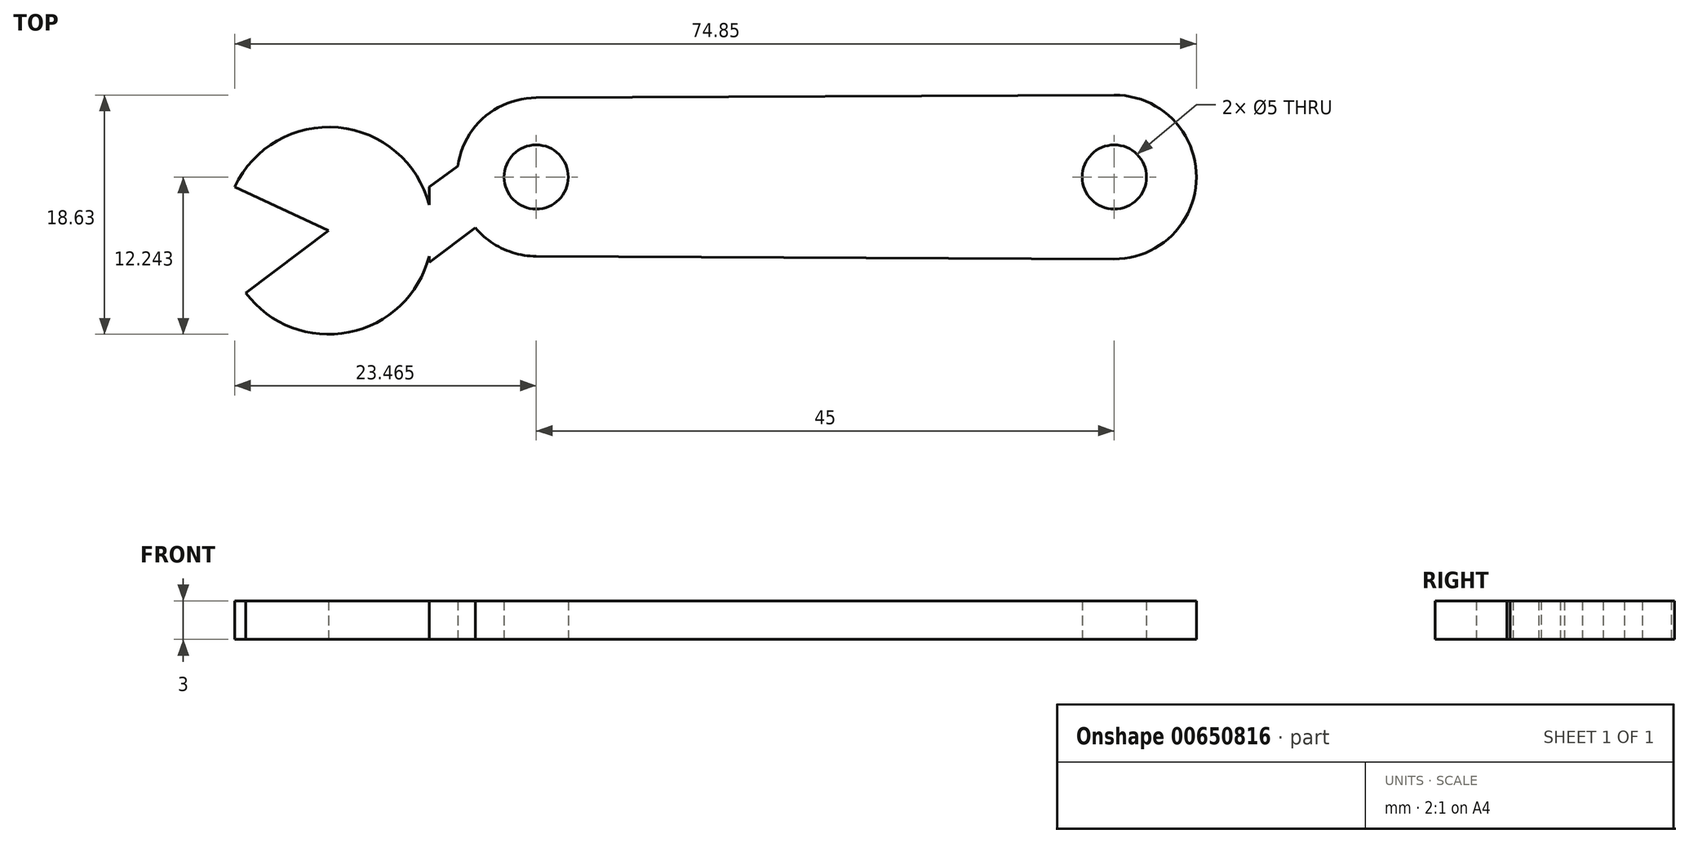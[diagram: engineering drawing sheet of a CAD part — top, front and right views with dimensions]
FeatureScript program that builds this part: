
annotation { "Feature Type Name" : "Feature", "Feature Type Description" : "" }
export const myFeature = defineFeature(function(context is Context, id is Id, definition is map)
    precondition{}
    {
        {
            var Q0;
            Q0=qCreatedBy(makeId("Top.planeOp"),FACE);
            var sketch = newSketch(context, id + "F0", { "sketchPlane" : qUnion([Q0])});
            skLineSegment(sketch, "E0", {"start": v(-64.62, 26.68) * mm, "end": v(-19.62, 26.68) * mm});
            skCircle(sketch, "E1", {"center": v(-19.62, 26.68) * mm, "radius": 6.39 * mm});
            skCircle(sketch, "E2", {"center": v(-64.62, 26.68) * mm, "radius": 6.17 * mm});
            skLineSegment(sketch, "E3", {"start": v(-64.62, 26.68) * mm, "end": v(-64.62, 20.52) * mm});
            skLineSegment(sketch, "E4", {"start": v(-64.62, 20.52) * mm, "end": v(-19.65, 20.3) * mm});
            skLineSegment(sketch, "E5", {"start": v(-19.65, 20.3) * mm, "end": v(-19.62, 26.68) * mm});
            skLineSegment(sketch, "E6", {"start": v(-19.62, 26.68) * mm, "end": v(-19.62, 33.07) * mm});
            skLineSegment(sketch, "E7", {"start": v(-19.62, 33.07) * mm, "end": v(-64.62, 32.85) * mm});
            skLineSegment(sketch, "E8", {"start": v(-64.62, 32.85) * mm, "end": v(-64.62, 26.68) * mm});
            skCircle(sketch, "E9", {"center": v(-64.62, 26.68) * mm, "radius": 1.67 * mm});
            skCircle(sketch, "E10", {"center": v(-19.62, 26.68) * mm, "radius": 1.58 * mm});
            skSolve(sketch);
        }
        {
            var Q0;
            {var subQ0=sQuery(id+"F0.wireOp",EDGE,"E1");var subQ2=sQuery(id+"F0.wireOp",EDGE,"E0");var subQ3=makeQuery(id+"F0.imprint","INTERSECT",VERTEX,{"derivedFrom":[subQ2,subQ0]});Q0=makeQuery(id+"F0.imprint","IMPRINT",FACE,{"disambiguationData":[TD([[makeQuery(id+"F0.imprint","IMPRINT",EDGE,{"disambiguationData":[TD([[subQ3,-1.0]])],"derivedFrom":subQ2}),1.0]])]});}
            var Q1;
            {var subQ0=sQuery(id+"F0.wireOp",EDGE,"E3");var subQ5=sQuery(id+"F0.wireOp",EDGE,"E9");var subQ7=makeQuery(id+"F0.imprint","INTERSECT",VERTEX,{"derivedFrom":[subQ0,subQ5]});Q1=makeQuery(id+"F0.imprint","IMPRINT",FACE,{"disambiguationData":[TD([[makeQuery(id+"F0.imprint","IMPRINT",EDGE,{"disambiguationData":[TD([[subQ7,1.0]])],"derivedFrom":subQ5}),-1.0]])]});}
            var Q2;
            {var subQ0=sQuery(id+"F0.wireOp",EDGE,"E9");var subQ1=sQuery(id+"F0.wireOp",EDGE,"E0");var subQ2=makeQuery(id+"F0.imprint","INTERSECT",VERTEX,{"derivedFrom":[subQ1,subQ0]});Q2=makeQuery(id+"F0.imprint","IMPRINT",FACE,{"disambiguationData":[TD([[makeQuery(id+"F0.imprint","IMPRINT",EDGE,{"disambiguationData":[TD([[subQ2,-1.0]])],"derivedFrom":subQ1}),-1.0]])]});}
            var Q3;
            {var subQ0=sQuery(id+"F0.wireOp",EDGE,"E1");var subQ1=sQuery(id+"F0.wireOp",EDGE,"E0");var subQ2=makeQuery(id+"F0.imprint","INTERSECT",VERTEX,{"derivedFrom":[subQ1,subQ0]});Q3=makeQuery(id+"F0.imprint","IMPRINT",FACE,{"disambiguationData":[TD([[makeQuery(id+"F0.imprint","IMPRINT",EDGE,{"disambiguationData":[TD([[subQ2,-1.0]])],"derivedFrom":subQ1}),-1.0]])]});}
            var Q4;
            {var subQ0=sQuery(id+"F0.wireOp",EDGE,"E9");var subQ1=sQuery(id+"F0.wireOp",EDGE,"E0");var subQ2=makeQuery(id+"F0.imprint","INTERSECT",VERTEX,{"derivedFrom":[subQ1,subQ0]});Q4=makeQuery(id+"F0.imprint","IMPRINT",FACE,{"disambiguationData":[TD([[makeQuery(id+"F0.imprint","IMPRINT",EDGE,{"disambiguationData":[TD([[subQ2,-1.0]])],"derivedFrom":subQ1}),1.0]])]});}
            var Q5;
            {var subQ5=sQuery(id+"F0.wireOp",EDGE,"E7");Q5=makeQuery(id+"F0.imprint","IMPRINT",FACE,{"disambiguationData":[TD([[makeQuery(id+"F0.imprint","IMPRINT",EDGE,{"derivedFrom":subQ5}),1.0]])]});}
            var Q6;
            {var subQ5=sQuery(id+"F0.wireOp",EDGE,"E4");Q6=makeQuery(id+"F0.imprint","IMPRINT",FACE,{"disambiguationData":[TD([[makeQuery(id+"F0.imprint","IMPRINT",EDGE,{"derivedFrom":subQ5}),1.0]])]});}
            var Q7;
            {var subQ1=sQuery(id+"F0.wireOp",EDGE,"E1");var subQ3=sQuery(id+"F0.wireOp",EDGE,"E6");var subQ4=makeQuery(id+"F0.imprint","INTERSECT",VERTEX,{"derivedFrom":[subQ1,subQ3]});Q7=makeQuery(id+"F0.imprint","IMPRINT",FACE,{"disambiguationData":[TD([[makeQuery(id+"F0.imprint","IMPRINT",EDGE,{"disambiguationData":[TD([[subQ4,1.0]])],"derivedFrom":subQ3}),-1.0]])]});}
            var Q8;
            {var subQ1=sQuery(id+"F0.wireOp",EDGE,"E0");var subQ3=sQuery(id+"F0.wireOp",EDGE,"E9");var subQ4=makeQuery(id+"F0.imprint","INTERSECT",VERTEX,{"derivedFrom":[subQ1,subQ3]});Q8=makeQuery(id+"F0.imprint","IMPRINT",FACE,{"disambiguationData":[TD([[makeQuery(id+"F0.imprint","IMPRINT",EDGE,{"disambiguationData":[TD([[subQ4,-1.0]])],"derivedFrom":subQ3}),1.0]])]});}
            var Q9;
            {var subQ1=sQuery(id+"F0.wireOp",EDGE,"E5");var subQ3=sQuery(id+"F0.wireOp",EDGE,"E10");var subQ4=makeQuery(id+"F0.imprint","INTERSECT",VERTEX,{"derivedFrom":[subQ1,subQ3]});Q9=makeQuery(id+"F0.imprint","IMPRINT",FACE,{"disambiguationData":[TD([[makeQuery(id+"F0.imprint","IMPRINT",EDGE,{"disambiguationData":[TD([[subQ4,-1.0]])],"derivedFrom":subQ3}),1.0]])]});}
            var Q10;
            {var subQ1=sQuery(id+"F0.wireOp",EDGE,"E3");var subQ3=sQuery(id+"F0.wireOp",EDGE,"E9");var subQ4=makeQuery(id+"F0.imprint","INTERSECT",VERTEX,{"derivedFrom":[subQ1,subQ3]});Q10=makeQuery(id+"F0.imprint","IMPRINT",FACE,{"disambiguationData":[TD([[makeQuery(id+"F0.imprint","IMPRINT",EDGE,{"disambiguationData":[TD([[subQ4,1.0]])],"derivedFrom":subQ3}),1.0]])]});}
            var Q11;
            {var subQ1=sQuery(id+"F0.wireOp",EDGE,"E0");var subQ3=sQuery(id+"F0.wireOp",EDGE,"E9");var subQ4=makeQuery(id+"F0.imprint","INTERSECT",VERTEX,{"derivedFrom":[subQ1,subQ3]});Q11=makeQuery(id+"F0.imprint","IMPRINT",FACE,{"disambiguationData":[TD([[makeQuery(id+"F0.imprint","IMPRINT",EDGE,{"disambiguationData":[TD([[subQ4,1.0]])],"derivedFrom":subQ3}),1.0]])]});}
            var Q12;
            {var subQ1=sQuery(id+"F0.wireOp",EDGE,"E0");var subQ3=sQuery(id+"F0.wireOp",EDGE,"E10");var subQ4=makeQuery(id+"F0.imprint","INTERSECT",VERTEX,{"derivedFrom":[subQ1,subQ3]});Q12=makeQuery(id+"F0.imprint","IMPRINT",FACE,{"disambiguationData":[TD([[makeQuery(id+"F0.imprint","IMPRINT",EDGE,{"disambiguationData":[TD([[subQ4,-1.0]])],"derivedFrom":subQ3}),1.0]])]});}
            var Q13;
            {var subQ1=sQuery(id+"F0.wireOp",EDGE,"E0");var subQ3=sQuery(id+"F0.wireOp",EDGE,"E10");var subQ4=makeQuery(id+"F0.imprint","INTERSECT",VERTEX,{"derivedFrom":[subQ1,subQ3]});Q13=makeQuery(id+"F0.imprint","IMPRINT",FACE,{"disambiguationData":[TD([[makeQuery(id+"F0.imprint","IMPRINT",EDGE,{"disambiguationData":[TD([[subQ4,1.0]])],"derivedFrom":subQ3}),1.0]])]});}
            extrude(context, id + "F1", {"entities" : qUnion([Q0, Q1, Q2, Q3, Q4, Q5, Q6, Q7, Q8, Q9, Q10, Q11, Q12, Q13]), "depth" : 3 * mm, "offsetDistance" : 25 * mm});
        }
        {
            var Q0;
            Q0=sQuery(id+"F0.wireOp",VERTEX,"E6.start");
            var Q1;
            Q1=sQuery(id+"F0.wireOp",VERTEX,"E9.center");
            var Q2;
            Q2=makeQuery(id+"F1.opExtrude","SWEPT_BODY",BODY,{"disambiguationData":[OSD([sQuery(id+"F0.wireOp",EDGE,"E1"),sQuery(id+"F0.wireOp",EDGE,"E2"),sQuery(id+"F0.wireOp",EDGE,"E4"),sQuery(id+"F0.wireOp",EDGE,"E7")])]});
            hole(context, id + "F2", {"style" : HoleStyle.SIMPLE, "endStyle" : HoleEndStyle.THROUGH, "oppositeDirection" : true, "holeDiameter" : 5 * mm, "majorDiameter" : 5 * mm, "isTappedThrough" : true, "tappedDepth" : 12 * mm, "tapClearance" : 3, "locations" : qUnion([Q0, Q1]), "scope" : qUnion([Q2])});
        }
        {
            var Q0;
            {var subQ0=sQuery(id+"F0.wireOp",EDGE,"E3");var subQ5=sQuery(id+"F0.wireOp",EDGE,"E9");var subQ7=makeQuery(id+"F0.imprint","INTERSECT",VERTEX,{"derivedFrom":[subQ0,subQ5]});Q0=makeQuery(id+"F0.imprint","IMPRINT",FACE,{"disambiguationData":[TD([[makeQuery(id+"F0.imprint","IMPRINT",EDGE,{"disambiguationData":[TD([[subQ7,1.0]])],"derivedFrom":subQ5}),-1.0]])]});}
            var sketch = newSketch(context, id + "F3", { "sketchPlane" : qUnion([Q0])});
            skLineSegment(sketch, "E11", {"start": v(-64.7, 31.84) * mm, "end": v(-72.95, 25.92) * mm});
            skLineSegment(sketch, "E12", {"start": v(-64.7, 26.23) * mm, "end": v(-72.95, 20.04) * mm});
            skLineSegment(sketch, "E13", {"start": v(-72.95, 20.04) * mm, "end": v(-72.95, 25.92) * mm});
            skCircle(sketch, "E14", {"center": v(-80.77, 22.5) * mm, "radius": 8.07 * mm});
            skLineSegment(sketch, "E15", {"start": v(-80.77, 22.5) * mm, "end": v(-87.22, 17.66) * mm});
            skLineSegment(sketch, "E16", {"start": v(-80.77, 22.5) * mm, "end": v(-88.08, 25.92) * mm});
            skSolve(sketch);
        }
        {
            var Q0;
            {var subQ0=sQuery(id+"F0.wireOp",EDGE,"E3");var subQ5=sQuery(id+"F0.wireOp",EDGE,"E9");var subQ7=makeQuery(id+"F0.imprint","INTERSECT",VERTEX,{"derivedFrom":[subQ0,subQ5]});Q0=makeQuery(id+"F0.imprint","IMPRINT",FACE,{"disambiguationData":[TD([[makeQuery(id+"F0.imprint","IMPRINT",EDGE,{"disambiguationData":[TD([[subQ7,1.0]])],"derivedFrom":subQ5}),-1.0]])]});}
            var Q1;
            {var subQ1=sQuery(id+"F0.wireOp",EDGE,"E3");var subQ3=sQuery(id+"F0.wireOp",EDGE,"E9");var subQ4=makeQuery(id+"F0.imprint","INTERSECT",VERTEX,{"derivedFrom":[subQ1,subQ3]});Q1=makeQuery(id+"F0.imprint","IMPRINT",FACE,{"disambiguationData":[TD([[makeQuery(id+"F0.imprint","IMPRINT",EDGE,{"disambiguationData":[TD([[subQ4,1.0]])],"derivedFrom":subQ3}),1.0]])]});}
            var Q2;
            {var subQ0=sQuery(id+"F3.wireOp",EDGE,"E13");var subQ1=sQuery(id+"F3.wireOp",EDGE,"E12");var subQ2=makeQuery(id+"F3.imprint","INTERSECT",VERTEX,{"derivedFrom":[subQ1,subQ0]});Q2=makeQuery(id+"F3.imprint","IMPRINT",FACE,{"disambiguationData":[TD([[makeQuery(id+"F3.imprint","IMPRINT",EDGE,{"disambiguationData":[TD([[subQ2,-1.0]])],"derivedFrom":subQ0}),-1.0]])]});}
            var Q3;
            {var subQ0=sQuery(id+"F3.wireOp",EDGE,"E15");Q3=makeQuery(id+"F3.imprint","IMPRINT",FACE,{"disambiguationData":[TD([[makeQuery(id+"F3.imprint","IMPRINT",EDGE,{"derivedFrom":subQ0}),1.0]])]});}
            var Q4;
            {var subQ1=sQuery(id+"F0.wireOp",EDGE,"E9");var subQ2=sQuery(id+"F0.wireOp",EDGE,"E3");var subQ3=makeQuery(id+"F0.imprint","INTERSECT",VERTEX,{"derivedFrom":[subQ2,subQ1]});var subQ11=makeQuery(id+"F0.imprint","IMPRINT",EDGE,{"disambiguationData":[TD([[subQ3,-1.0]])],"derivedFrom":subQ2});Q4=makeQuery(id+"F3.imprint","IMPRINT",FACE,{"disambiguationData":[TD([[makeQuery(id+"F3.imprint","IMPRINT",EDGE,{"derivedFrom":subQ11}),-1.0]])]});}
            var Q5;
            {var subQ0=sQuery(id+"F0.wireOp",EDGE,"E8");var subQ3=sQuery(id+"F0.wireOp",EDGE,"E9");var subQ4=makeQuery(id+"F0.imprint","INTERSECT",VERTEX,{"derivedFrom":[subQ0,subQ3]});var subQ5=makeQuery(id+"F0.imprint","IMPRINT",EDGE,{"disambiguationData":[TD([[subQ4,1.0]])],"derivedFrom":subQ0});Q5=makeQuery(id+"F3.imprint","IMPRINT",FACE,{"disambiguationData":[TD([[makeQuery(id+"F3.imprint","IMPRINT",EDGE,{"derivedFrom":subQ5}),-1.0]])]});}
            var Q6;
            {var subQ0=sQuery(id+"F3.wireOp",EDGE,"E14");var subQ1=sQuery(id+"F3.wireOp",EDGE,"E13");var subQ2=makeQuery(id+"F3.imprint","INTERSECT",VERTEX,{"disambiguationData":[OD(0.0)],"derivedFrom":[subQ1,subQ0]});Q6=makeQuery(id+"F3.imprint","IMPRINT",FACE,{"disambiguationData":[TD([[makeQuery(id+"F3.imprint","IMPRINT",EDGE,{"disambiguationData":[TD([[subQ2,-1.0]])],"derivedFrom":subQ1}),-1.0]])]});}
            extrude(context, id + "F4", {"entities" : qUnion([Q0, Q1, Q2, Q3, Q4, Q5, Q6]), "operationType" : NewBodyOperationType.ADD, "depth" : 3 * mm, "offsetDistance" : 25 * mm});
        }
        {
            var Q0;
            Q0=sQuery(id+"F0.wireOp",VERTEX,"E0.start");
            var Q1;
            Q1=makeQuery(id+"F1.opExtrude","SWEPT_BODY",BODY,{"disambiguationData":[OSD([sQuery(id+"F0.wireOp",EDGE,"E1"),sQuery(id+"F0.wireOp",EDGE,"E2"),sQuery(id+"F0.wireOp",EDGE,"E4"),sQuery(id+"F0.wireOp",EDGE,"E7")])]});
            hole(context, id + "F5", {"style" : HoleStyle.SIMPLE, "endStyle" : HoleEndStyle.THROUGH, "oppositeDirection" : true, "holeDiameter" : 5 * mm, "majorDiameter" : 5 * mm, "isTappedThrough" : true, "tappedDepth" : 12 * mm, "tapClearance" : 3, "locations" : qUnion([Q0]), "scope" : qUnion([Q1])});
        }
    });
